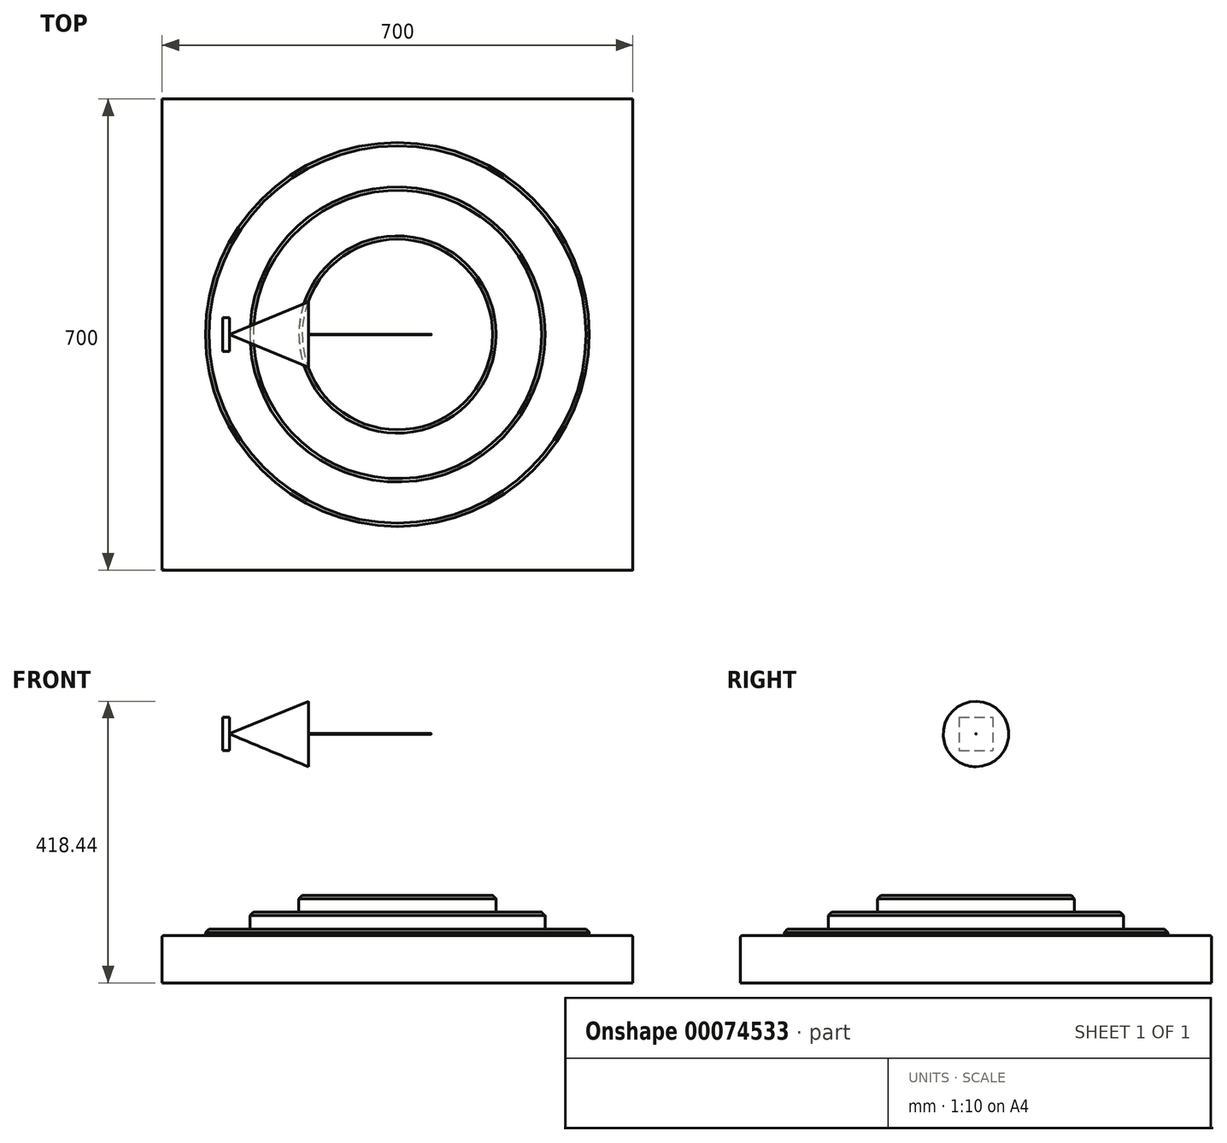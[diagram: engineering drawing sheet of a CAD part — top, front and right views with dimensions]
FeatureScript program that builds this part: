
annotation { "Feature Type Name" : "Feature", "Feature Type Description" : "" }
export const myFeature = defineFeature(function(context is Context, id is Id, definition is map)
    precondition{}
    {
        {
            var Q0;
            Q0=qCreatedBy(makeId("Top.planeOp"),FACE);
            var sketch = newSketch(context, id + "F0", { "sketchPlane" : qUnion([Q0])});
            skLineSegment(sketch, "E0.rect.bottom", {"start": v(-350, 350) * mm, "end": v(350, 350) * mm});
            skLineSegment(sketch, "E0.rect.top", {"start": v(-350, -350) * mm, "end": v(350, -350) * mm});
            skLineSegment(sketch, "E0.rect.left", {"start": v(-350, 350) * mm, "end": v(-350, -350) * mm});
            skLineSegment(sketch, "E0.rect.right", {"start": v(350, 350) * mm, "end": v(350, -350) * mm});
            skPoint(sketch, "E0.rect.middle", {"position": v(0, 0) * mm});
            skSolve(sketch);
        }
        {
            var Q0;
            Q0=makeQuery(id+"F0.imprint","IMPRINT",FACE,{"disambiguationData":[TD([[makeQuery(id+"F0.imprint","IMPRINT",EDGE,{"derivedFrom":sQuery(id+"F0.wireOp",EDGE,"E0.rect.bottom")}),-1.0]])]});
            extrude(context, id + "F1", {"entities" : qUnion([Q0]), "oppositeDirection" : true, "depth" : 70 * mm});
        }
        {
            var Q0;
            Q0=makeQuery(id+"F1.opExtrude","CAP_FACE",FACE,{"disambiguationData":[OSD([sQuery(id+"F0.wireOp",EDGE,"E0.rect.bottom"),sQuery(id+"F0.wireOp",EDGE,"E0.rect.top"),sQuery(id+"F0.wireOp",EDGE,"E0.rect.left"),sQuery(id+"F0.wireOp",EDGE,"E0.rect.right")])],"isStart":true});
            var sketch = newSketch(context, id + "F2", { "sketchPlane" : qUnion([Q0])});
            skCircle(sketch, "E1", {"center": v(0, 0) * mm, "radius": 285.19 * mm});
            skSolve(sketch);
        }
        {
            var Q0;
            Q0=makeQuery(id+"F2.imprint","IMPRINT",FACE,{"disambiguationData":[TD([[makeQuery(id+"F2.imprint","IMPRINT",EDGE,{"derivedFrom":sQuery(id+"F2.wireOp",EDGE,"E1")}),1.0]])]});
            extrude(context, id + "F3", {"entities" : qUnion([Q0]), "operationType" : NewBodyOperationType.ADD, "depth" : 10 * mm});
        }
        {
            var Q0;
            Q0=makeQuery(id+"F3.opExtrude","CAP_FACE",FACE,{"disambiguationData":[OSD([sQuery(id+"F2.wireOp",EDGE,"E1")])],"isStart":false});
            var sketch = newSketch(context, id + "F4", { "sketchPlane" : qUnion([Q0])});
            skCircle(sketch, "E2", {"center": v(0, 0) * mm, "radius": 219.2 * mm});
            skSolve(sketch);
        }
        {
            var Q0;
            Q0=makeQuery(id+"F4.imprint","IMPRINT",FACE,{"disambiguationData":[TD([[makeQuery(id+"F4.imprint","IMPRINT",EDGE,{"derivedFrom":sQuery(id+"F4.wireOp",EDGE,"E2")}),1.0]])]});
            extrude(context, id + "F5", {"entities" : qUnion([Q0]), "operationType" : NewBodyOperationType.ADD, "depth" : 25 * mm});
        }
        {
            var Q0;
            Q0=makeQuery(id+"F5.opExtrude","CAP_FACE",FACE,{"disambiguationData":[OSD([sQuery(id+"F4.wireOp",EDGE,"E2")])],"isStart":false});
            var sketch = newSketch(context, id + "F6", { "sketchPlane" : qUnion([Q0])});
            skCircle(sketch, "E3", {"center": v(0, 0) * mm, "radius": 146.56 * mm});
            skSolve(sketch);
        }
        {
            var Q0;
            Q0=makeQuery(id+"F6.imprint","IMPRINT",FACE,{"disambiguationData":[TD([[makeQuery(id+"F6.imprint","IMPRINT",EDGE,{"derivedFrom":sQuery(id+"F6.wireOp",EDGE,"E3")}),1.0]])]});
            extrude(context, id + "F7", {"entities" : qUnion([Q0]), "operationType" : NewBodyOperationType.ADD, "depth" : 25 * mm});
        }
        {
            var Q0;
            Q0=qCreatedBy(makeId("Right.planeOp"),FACE);
            cPlane(context, id + "F8", {"entities" : qUnion([Q0]), "cplaneType" : CPlaneType.OFFSET, "offset" : 250 * mm, "oppositeDirection" : true, "width" : 150 * mm, "height" : 150 * mm});
        }
        {
            var Q0;
            Q0=qCreatedBy(id+"F8.planeOp",FACE);
            var sketch = newSketch(context, id + "F9", { "sketchPlane" : qUnion([Q0])});
            skLineSegment(sketch, "E4.rect.bottom", {"start": v(-25, 325) * mm, "end": v(25, 325) * mm});
            skLineSegment(sketch, "E4.rect.top", {"start": v(-25, 275) * mm, "end": v(25, 275) * mm});
            skLineSegment(sketch, "E4.rect.left", {"start": v(-25, 325) * mm, "end": v(-25, 275) * mm});
            skLineSegment(sketch, "E4.rect.right", {"start": v(25, 325) * mm, "end": v(25, 275) * mm});
            skPoint(sketch, "E4.rect.middle", {"position": v(0, 300) * mm});
            skSolve(sketch);
        }
        {
            var Q0;
            Q0=makeQuery(id+"F9.imprint","IMPRINT",FACE,{"disambiguationData":[TD([[makeQuery(id+"F9.imprint","IMPRINT",EDGE,{"derivedFrom":sQuery(id+"F9.wireOp",EDGE,"E4.rect.bottom")}),-1.0]])]});
            extrude(context, id + "F10", {"entities" : qUnion([Q0]), "oppositeDirection" : true, "depth" : 10 * mm});
        }
        {
            var Q0;
            Q0=makeQuery(id+"F10.opExtrude","CAP_FACE",FACE,{"disambiguationData":[OSD([sQuery(id+"F9.wireOp",EDGE,"E4.rect.bottom"),sQuery(id+"F9.wireOp",EDGE,"E4.rect.top"),sQuery(id+"F9.wireOp",EDGE,"E4.rect.left"),sQuery(id+"F9.wireOp",EDGE,"E4.rect.right")])],"isStart":true});
            var sketch = newSketch(context, id + "F11", { "sketchPlane" : qUnion([Q0])});
            skCircle(sketch, "E5", {"center": v(0, 300) * mm, "radius": 0.5 * mm});
            skSolve(sketch);
        }
        {
            var Q0;
            Q0=makeQuery(id+"F11.imprint","IMPRINT",FACE,{"disambiguationData":[TD([[makeQuery(id+"F11.imprint","IMPRINT",EDGE,{"derivedFrom":sQuery(id+"F11.wireOp",EDGE,"E5")}),1.0]])]});
            extrude(context, id + "F12", {"entities" : qUnion([Q0]), "operationType" : NewBodyOperationType.ADD, "depth" : 300 * mm});
        }
        {
            var Q0;
            Q0=makeQuery(id+"F7.opExtrude","CAP_EDGE",EDGE,{"disambiguationData":[OSD([sQuery(id+"F6.wireOp",EDGE,"E3")])],"isStart":false});
            var Q1;
            Q1=makeQuery(id+"F5.opExtrude","CAP_EDGE",EDGE,{"disambiguationData":[OSD([sQuery(id+"F4.wireOp",EDGE,"E2")])],"isStart":false});
            var Q2;
            Q2=makeQuery(id+"F3.opExtrude","CAP_EDGE",EDGE,{"disambiguationData":[OSD([sQuery(id+"F2.wireOp",EDGE,"E1")])],"isStart":false});
            chamfer(context, id + "F13", {"entities" : qUnion([Q0, Q1, Q2]), "width" : 5 * mm, "tangentPropagation" : true});
        }
        {
            var Q0;
            Q0=makeQuery(id+"F1.opExtrude","CAP_EDGE",EDGE,{"disambiguationData":[OSD([sQuery(id+"F0.wireOp",EDGE,"E0.rect.top")])],"isStart":true});
            var Q1;
            Q1=makeQuery(id+"F1.opExtrude","CAP_FACE",FACE,{"disambiguationData":[OSD([sQuery(id+"F0.wireOp",EDGE,"E0.rect.bottom"),sQuery(id+"F0.wireOp",EDGE,"E0.rect.top"),sQuery(id+"F0.wireOp",EDGE,"E0.rect.left"),sQuery(id+"F0.wireOp",EDGE,"E0.rect.right")])],"isStart":true});
            fillet(context, id + "F14", {"entities" : qUnion([Q0, Q1]), "radius" : 2 * mm, "tangentPropagation" : true, "allowEdgeOverflow" : false});
        }
        {
            var Q0;
            Q0=qCreatedBy(makeId("Front.planeOp"),FACE);
            var sketch = newSketch(context, id + "F15", { "sketchPlane" : qUnion([Q0])});
            skLineSegment(sketch, "E6", {"start": v(-250.01, 300.01) * mm, "end": v(-132.32, 348.44) * mm});
            skLineSegment(sketch, "E7", {"start": v(-132.32, 348.44) * mm, "end": v(-132.32, 299.74) * mm});
            skLineSegment(sketch, "E8", {"start": v(-132.32, 299.74) * mm, "end": v(-250.01, 300.01) * mm});
            skSolve(sketch);
        }
        {
            var Q0;
            Q0=makeQuery(id+"F15.imprint","IMPRINT",FACE,{"disambiguationData":[TD([[makeQuery(id+"F15.imprint","IMPRINT",EDGE,{"derivedFrom":sQuery(id+"F15.wireOp",EDGE,"E6")}),-1.0]])]});
            var Q1;
            Q1=sQuery(id+"F15.wireOp",EDGE,"E8");
            revolve(context, id + "F16", {"operationType" : NewBodyOperationType.ADD, "entities" : qUnion([Q0]), "axis" : qUnion([Q1]), "revolveType" : RevolveType.FULL});
        }
    });
